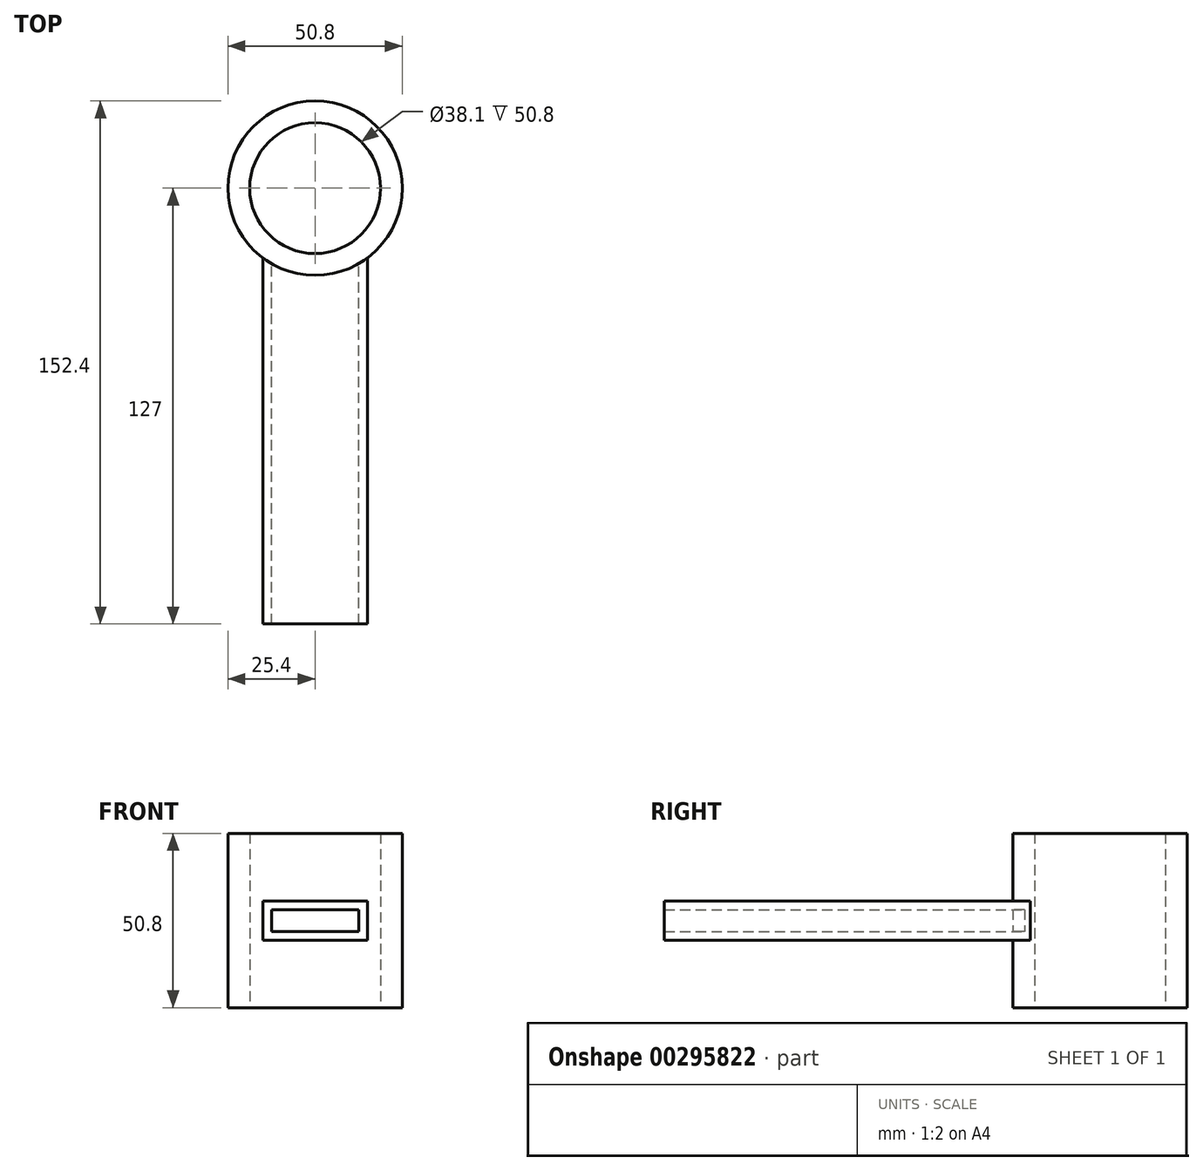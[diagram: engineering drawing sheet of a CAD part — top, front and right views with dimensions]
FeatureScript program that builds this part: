
annotation { "Feature Type Name" : "Feature", "Feature Type Description" : "" }
export const myFeature = defineFeature(function(context is Context, id is Id, definition is map)
    precondition{}
    {
        {
            var Q0;
            Q0=qCreatedBy(makeId("Top.planeOp"),FACE);
            var sketch = newSketch(context, id + "F0", { "sketchPlane" : qUnion([Q0])});
            skCircle(sketch, "E0", {"center": v(0, 0) * mm, "radius": 19.05 * mm});
            skCircle(sketch, "E1", {"center": v(0, 0) * mm, "radius": 25.4 * mm});
            skPoint(sketch, "E2", {"position": v(0, -25.4) * mm});
            skSolve(sketch);
        }
        {
            var Q0;
            Q0 = qSketchRegion(id + "F0", true);
            extrude(context, id + "F1", {"entities" : qUnion([Q0]), "depth" : 25.4 * mm, "hasSecondDirection" : true, "secondDirectionOppositeDirection" : true, "secondDirectionDepth" : 25.4 * mm});
        }
        {
            var Q0;
            Q0=qCreatedBy(makeId("Front.planeOp"),FACE);
            var sketch = newSketch(context, id + "F2", { "sketchPlane" : qUnion([Q0])});
            skLineSegment(sketch, "E3.bottom", {"start": v(12.7, 3.18) * mm, "end": v(-12.7, 3.18) * mm});
            skLineSegment(sketch, "E3.top", {"start": v(12.7, -3.18) * mm, "end": v(-12.7, -3.18) * mm});
            skLineSegment(sketch, "E3.left", {"start": v(12.7, 3.18) * mm, "end": v(12.7, -3.18) * mm});
            skLineSegment(sketch, "E3.right", {"start": v(-12.7, 3.18) * mm, "end": v(-12.7, -3.18) * mm});
            skPoint(sketch, "E3.middle", {"position": v(0, 0) * mm});
            skLineSegment(sketch, "E4.bottom", {"start": v(15.24, 5.72) * mm, "end": v(-15.24, 5.72) * mm});
            skLineSegment(sketch, "E4.top", {"start": v(15.24, -5.72) * mm, "end": v(-15.24, -5.72) * mm});
            skLineSegment(sketch, "E4.left", {"start": v(15.24, 5.72) * mm, "end": v(15.24, -5.72) * mm});
            skLineSegment(sketch, "E4.right", {"start": v(-15.24, 5.72) * mm, "end": v(-15.24, -5.72) * mm});
            skSolve(sketch);
        }
        {
            var Q0;
            Q0=makeQuery(id+"F2.imprint","IMPRINT",FACE,{"disambiguationData":[TD([[makeQuery(id+"F2.imprint","IMPRINT",EDGE,{"derivedFrom":sQuery(id+"F2.wireOp",EDGE,"E3.bottom")}),-1.0]])]});
            extrude(context, id + "F3", {"entities" : qUnion([Q0]), "operationType" : NewBodyOperationType.ADD, "depth" : 127 * mm});
        }
        {
            var Q0;
            Q0=makeQuery(id+"F0.imprint","IMPRINT",FACE,{"disambiguationData":[TD([[makeQuery(id+"F0.imprint","IMPRINT",EDGE,{"derivedFrom":sQuery(id+"F0.wireOp",EDGE,"E0")}),1.0]])]});
            extrude(context, id + "F4", {"entities" : qUnion([Q0]), "operationType" : NewBodyOperationType.REMOVE, "endBound" : BoundingType.THROUGH_ALL, "oppositeDirection" : true, "depth" : 25.4 * mm, "hasSecondDirection" : true, "secondDirectionBound" : SecondDirectionBoundingType.THROUGH_ALL, "secondDirectionOppositeDirection" : false, "secondDirectionDepth" : 25.4 * mm});
        }
    });
